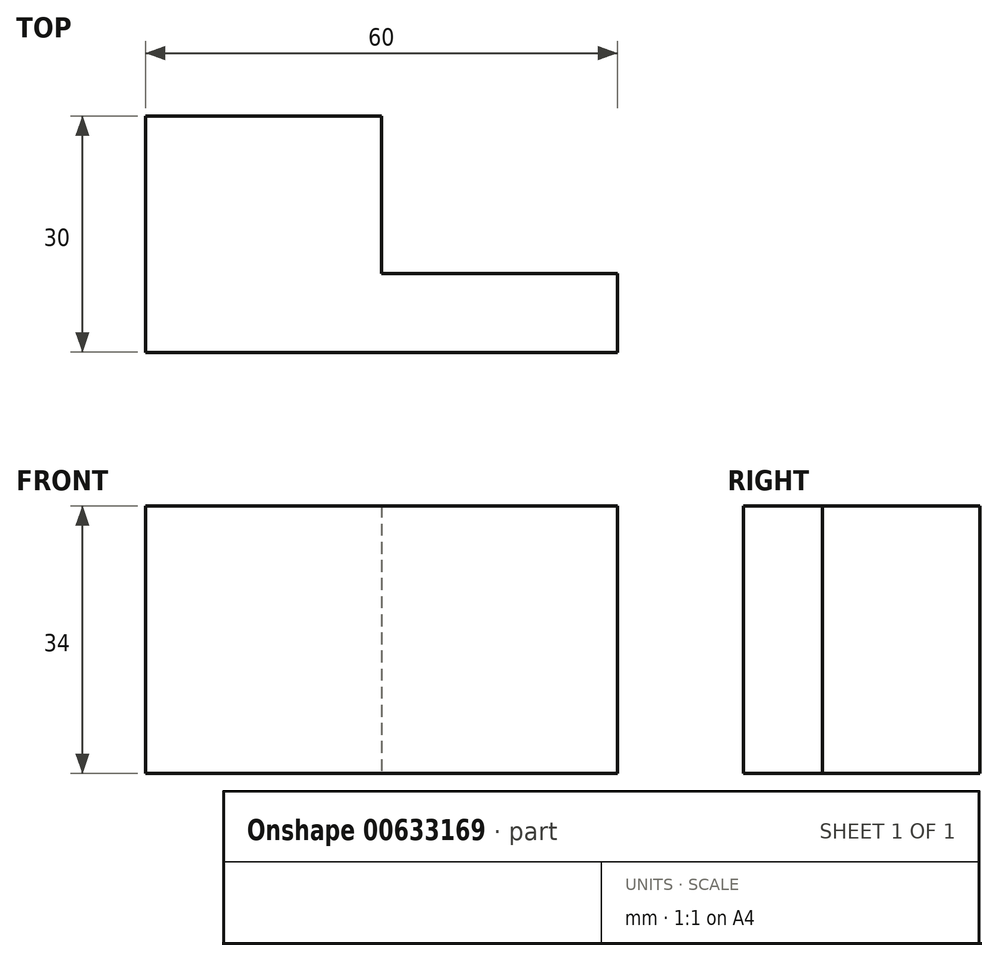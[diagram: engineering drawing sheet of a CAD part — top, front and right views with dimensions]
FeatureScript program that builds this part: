
annotation { "Feature Type Name" : "Feature", "Feature Type Description" : "" }
export const myFeature = defineFeature(function(context is Context, id is Id, definition is map)
    precondition{}
    {
        {
            var Q0;
            Q0=qCreatedBy(makeId("Top.planeOp"),FACE);
            var sketch = newSketch(context, id + "F0", { "sketchPlane" : qUnion([Q0])});
            skLineSegment(sketch, "E0", {"start": v(0, 0) * mm, "end": v(0, 26.75) * mm, "construction": true});
            skLineSegment(sketch, "E1", {"start": v(0, 0) * mm, "end": v(0, -32.88) * mm});
            skLineSegment(sketch, "E2", {"start": v(-15, 3.67) * mm, "end": v(15, 3.67) * mm});
            skLineSegment(sketch, "E3", {"start": v(15, 3.67) * mm, "end": v(15, -16.33) * mm});
            skLineSegment(sketch, "E4", {"start": v(15, -16.33) * mm, "end": v(45, -16.33) * mm});
            skLineSegment(sketch, "E5", {"start": v(45, -16.33) * mm, "end": v(45, -26.33) * mm});
            skLineSegment(sketch, "E6", {"start": v(45, -26.33) * mm, "end": v(-15, -26.33) * mm});
            skLineSegment(sketch, "E7", {"start": v(-15, -26.33) * mm, "end": v(-15, 3.67) * mm});
            skSolve(sketch);
        }
        {
            var Q0;
            Q0=makeQuery(id+"F0.imprint","IMPRINT",FACE,{"disambiguationData":[TD([[makeQuery(id+"F0.imprint","IMPRINT",EDGE,{"derivedFrom":sQuery(id+"F0.wireOp",EDGE,"E2")}),-1.0]])]});
            extrude(context, id + "F1", {"entities" : qUnion([Q0]), "depth" : 34 * mm, "offsetDistance" : 25 * mm});
        }
    });
